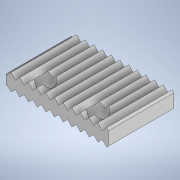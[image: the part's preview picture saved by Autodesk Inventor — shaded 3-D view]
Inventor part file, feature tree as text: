
AUTODESK INVENTOR PART (.ipt)
format: ipt  version: 2020 (Build 240168000, 168)  size: 337,408 bytes
history: native  units: in
note: dims shown in document units (in); Inventor stores cm internally (conversion verified against a paired STEP export)
features: extrude x4, sketch x4, mirror x1
ambient origin geometry x8: Origin, YZ Plane, XZ Plane, XY Plane, X Axis, Y Axis, Z Axis, Center Point
bodies: Solid1 (feature_tree)
feature tree (9):
  extrude  "Extrusion1"  Depth=0.6299in
  extrude  "Extrusion2"  Depth=0.0591in
  extrude  "Extrusion4"  TaperAngle=45.0deg  [1 undecoded]
  extrude  "Extrusion5"  Depth=0.0591in
  mirror  "Mirror1"
  sketch  "Sketch1"  dims[d0=1.8898in d1=0.6299in]
  sketch  "Sketch2"  dims[d2=0.0394in d3=0.0in d6=0.0591in]
  sketch  "Sketch4"  dims[d7=0.0591in d8=45.0deg]
  sketch  "Sketch5"  dims[d9=0.0591in d10=0.0591in d11=90.0deg d12=0.0591in d13=0.0591in d14=0.0591in d15=0.0591in d16=45.0deg d17=0.0591in d18=90.0deg d19=0.0591in d20=0.0591in d21=0.0591in d22=0.0591in d23=0.0591in d24=0.0591in d25=90.0deg d26=0.0591in d27=90.0deg d28=0.0591in d29=90.0deg d30=0.0591in d31=0.0591in d32=0.0591in d33=0.0591in d34=90.0deg d35=0.0591in d36=90.0deg d37=0.0591in d38=90.0deg d39=0.0591in d40=90.0deg d41=0.0591in d42=90.0deg d43=0.0591in d44=90.0deg d45=0.0591in d46=45.0deg d47=0.0591in d48=90.0deg d49=0.0591in d50=90.0deg d51=0.0591in d52=90.0deg d53=0.0591in d54=90.0deg d55=0.0591in d56=90.0deg d57=0.0591in d58=90.0deg d59=0.0591in d60=90.0deg d61=0.0591in d62=90.0deg d63=0.0591in d64=90.0deg d65=0.0591in d66=90.0deg d67=0.0591in d68=90.0deg d69=0.0591in d70=90.0deg d71=0.0591in d72=90.0deg d73=0.0591in d74=90.0deg d75=0.0591in d76=90.0deg d77=0.0591in d78=90.0deg d79=0.0591in d80=90.0deg d81=0.0591in d82=90.0deg d83=0.0591in d84=90.0deg d85=0.6299in d86=0.0in d93=0.9843in d94=0.6299in d95=0.3937in d96=0.0in d97=0.1575in d98=0.1575in d99=0.3937in d100=0.0in d101=0.0197in d102=0.0344in d103=0.0197in d104=0.0344in]
note: 1 required parameter value undecoded (feature->parameter linkage not recoverable at this tier; creation-order binding heuristic only, values carry confidence <= 0.55)
